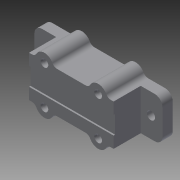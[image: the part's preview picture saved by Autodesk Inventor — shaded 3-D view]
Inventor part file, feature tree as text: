
AUTODESK INVENTOR PART (.ipt)
format: ipt  version: 2015 (Build 190159000, 159)  size: 171,008 bytes
history: native  units: mm
features: sketch x4, extrude x3, hole x2, fillet x2
ambient origin geometry x8: Origin, YZ Plane, XZ Plane, XY Plane, X Axis, Y Axis, Z Axis, Center Point
bodies: Body1 (feature_tree)
feature tree (11):
  sketch  "Sketch1"  dims[d0=16.0mm d1=50.0mm]
  extrude  "Extrusion2"  Depth=50.0mm
  extrude  "Extrusion3"  Depth=7.0mm
  hole  "Hole1"  [1 undecoded]
  hole  "Hole2"  [1 undecoded]
  fillet  "Fillet1"  Radius=2.0mm
  fillet  "Fillet2"  Radius=3.0mm
  extrude  "Extrusion4"  Depth=0.6mm
  sketch  "Sketch2"  dims[d4=21.0mm d5=7.0mm]
  sketch  "Sketch3"  dims[d6=14.6mm d7=0.0mm d8=8.5mm]
  sketch  "Sketch4"  dims[d9=10.6mm d10=0.0mm d12=20.49mm d13=3.2mm d14=6.0mm d15=4.0mm d16=2.0mm d17=45.0deg d18=8.0mm d19=20.594885mm d20=2.4mm d21=6.0mm d22=3.0mm d23=2.0mm d24=45.0deg d25=8.0mm d26=20.594885mm d27=2.0mm d28=3.0mm d31=15.0mm d32=7.0mm d33=0.6mm d34=0.0mm]
note: 2 required parameter values undecoded (feature->parameter linkage not recoverable at this tier; creation-order binding heuristic only, values carry confidence <= 0.55)
